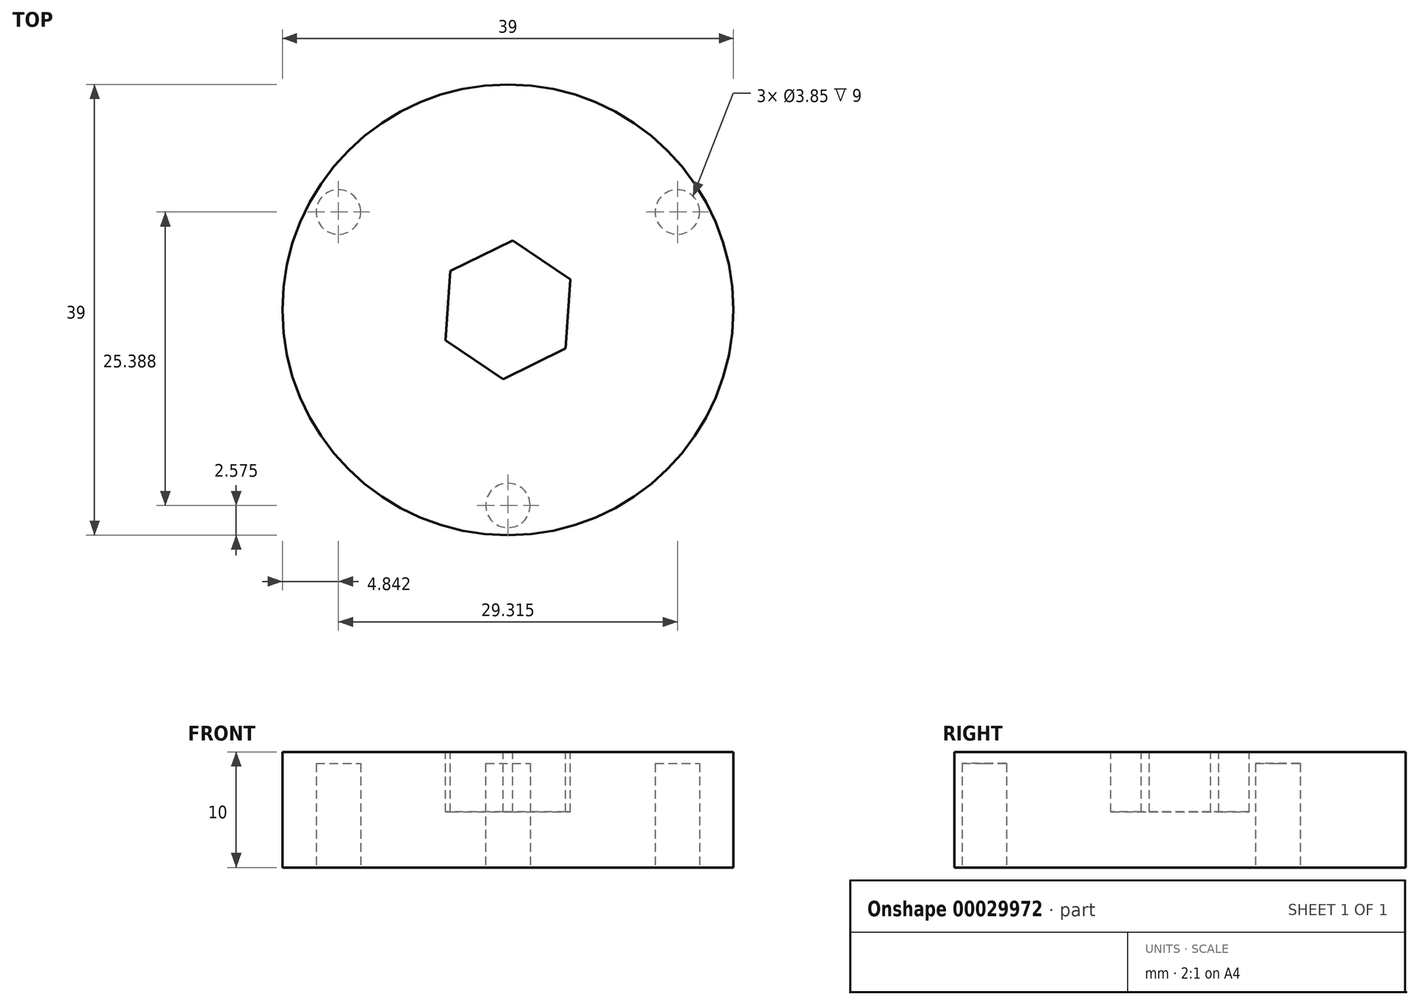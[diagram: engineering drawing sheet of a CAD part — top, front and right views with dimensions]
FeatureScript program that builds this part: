
annotation { "Feature Type Name" : "Feature", "Feature Type Description" : "" }
export const myFeature = defineFeature(function(context is Context, id is Id, definition is map)
    precondition{}
    {
        {
            var Q0;
            Q0=qCreatedBy(makeId("Top.planeOp"),FACE);
            var sketch = newSketch(context, id + "F0", { "sketchPlane" : qUnion([Q0])});
            skCircle(sketch, "E0", {"center": v(0, 0) * mm, "radius": 19.5 * mm});
            skSolve(sketch);
        }
        {
            var Q0;
            Q0 = qSketchRegion(id + "F0", true);
            extrude(context, id + "F1", {"entities" : qUnion([Q0]), "depth" : 10 * mm});
        }
        {
            var Q0;
            Q0=makeQuery(id+"F1.opExtrude","CAP_FACE",FACE,{"disambiguationData":[OSD([sQuery(id+"F0.wireOp",EDGE,"E0")])],"isStart":false});
            var sketch = newSketch(context, id + "F2", { "sketchPlane" : qUnion([Q0])});
            skCircle(sketch, "E1.cCircle", {"center": v(0, 0) * mm, "radius": 5.2 * mm, "construction": true});
            skLineSegment(sketch, "E1.0", {"start": v(4.98, -3.35) * mm, "end": v(-0.4, -6) * mm});
            skLineSegment(sketch, "E1.1", {"start": v(-0.4, -6) * mm, "end": v(-5.4, -2.64) * mm});
            skLineSegment(sketch, "E1.2", {"start": v(-5.4, -2.64) * mm, "end": v(-4.98, 3.35) * mm});
            skLineSegment(sketch, "E1.3", {"start": v(-4.98, 3.35) * mm, "end": v(0.4, 6) * mm});
            skLineSegment(sketch, "E1.4", {"start": v(0.4, 6) * mm, "end": v(5.4, 2.64) * mm});
            skLineSegment(sketch, "E1.5", {"start": v(5.4, 2.64) * mm, "end": v(4.98, -3.35) * mm});
            skPoint(sketch, "E1.0.midPoint", {"position": v(2.29, -4.67) * mm});
            skSolve(sketch);
        }
        {
            var Q0;
            Q0 = qSketchRegion(id + "F2", true);
            extrude(context, id + "F3", {"entities" : qUnion([Q0]), "operationType" : NewBodyOperationType.REMOVE, "oppositeDirection" : true, "depth" : 5.2 * mm});
        }
        {
            var Q0;
            Q0=makeQuery(id+"F1.opExtrude","CAP_FACE",FACE,{"disambiguationData":[OSD([sQuery(id+"F0.wireOp",EDGE,"E0")])],"isStart":true});
            var sketch = newSketch(context, id + "F4", { "sketchPlane" : qUnion([Q0])});
            skCircle(sketch, "E2", {"center": v(0, 16.93) * mm, "radius": 1.93 * mm});
            skCircle(sketch, "E3.1.0", {"center": v(-14.66, -8.46) * mm, "radius": 1.93 * mm});
            skCircle(sketch, "E3.2.0", {"center": v(14.66, -8.46) * mm, "radius": 1.93 * mm});
            skPoint(sketch, "E3.center", {"position": v(0, 0) * mm});
            skSolve(sketch);
        }
        {
            var Q0;
            Q0=makeQuery(id+"F4.imprint","IMPRINT",FACE,{"disambiguationData":[TD([[makeQuery(id+"F4.imprint","IMPRINT",EDGE,{"derivedFrom":sQuery(id+"F4.wireOp",EDGE,"E2")}),1.0]])]});
            var Q1;
            Q1=makeQuery(id+"F4.imprint","IMPRINT",FACE,{"disambiguationData":[TD([[makeQuery(id+"F4.imprint","IMPRINT",EDGE,{"derivedFrom":sQuery(id+"F4.wireOp",EDGE,"E3.1.0")}),1.0]])]});
            var Q2;
            Q2=makeQuery(id+"F4.imprint","IMPRINT",FACE,{"disambiguationData":[TD([[makeQuery(id+"F4.imprint","IMPRINT",EDGE,{"derivedFrom":sQuery(id+"F4.wireOp",EDGE,"E3.2.0")}),1.0]])]});
            extrude(context, id + "F5", {"entities" : qUnion([Q0, Q1, Q2]), "operationType" : NewBodyOperationType.REMOVE, "oppositeDirection" : true, "depth" : 9 * mm});
        }
    });
